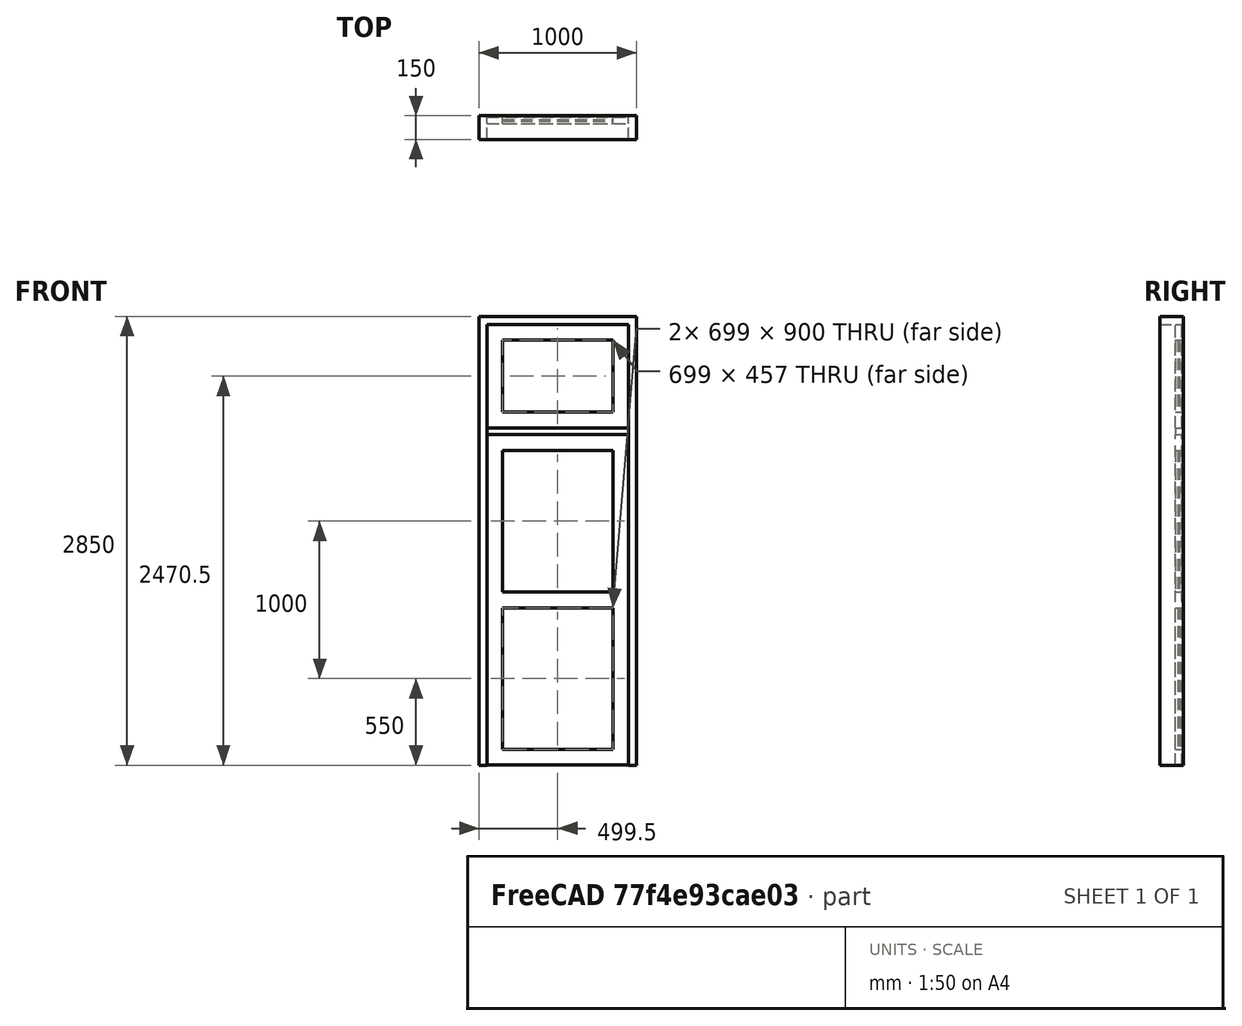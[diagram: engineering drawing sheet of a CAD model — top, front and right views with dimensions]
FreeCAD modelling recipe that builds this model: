
FCSTD DOCUMENT  (FreeCAD 0.16R6704 (Git))
Label: Single door with glass and transom
License: CreativeCommons Attribution
LicenseURL: http://creativecommons.org/licenses/by/4.0/
objects: Sketcher::SketchObject×1, Part::FeaturePython×1
note: 2 computed .brp shape members not serialized (recipe doc carries the construction recipe); baked Part::Feature solids carry a one-line shape summary decoded from their .brp

FEATURE [Sketcher::SketchObject] Sketch177  label="Sketch"
  Placement = pos=(0,0,0) rot=(1,0,0;1.5708rad)
  sketch-geometry (33):
    g0: LineSegment StartX=0 StartY=0 StartZ=0 EndX=1000 EndY=0 EndZ=0
    g1: LineSegment StartX=1000 StartY=0 StartZ=0 EndX=1000 EndY=2850 EndZ=0
    g2: LineSegment StartX=1000 StartY=2850 StartZ=0 EndX=0 EndY=2850 EndZ=0
    g3: LineSegment StartX=0 StartY=2850 StartZ=0 EndX=0 EndY=0 EndZ=0
    g4: LineSegment StartX=50 StartY=0 StartZ=0 EndX=950 EndY=0 EndZ=0
    g5: LineSegment StartX=950 StartY=0 StartZ=0 EndX=950 EndY=2800 EndZ=0
    g6: LineSegment StartX=950 StartY=2800 StartZ=0 EndX=50 EndY=2800 EndZ=0
    g7: LineSegment StartX=50 StartY=2800 StartZ=0 EndX=50 EndY=0 EndZ=0
    g8: LineSegment StartX=150 StartY=2000 StartZ=0 EndX=849 EndY=2000 EndZ=0
    g9: LineSegment StartX=849 StartY=2000 StartZ=0 EndX=849 EndY=1100 EndZ=0
    g10: LineSegment StartX=849 StartY=1100 StartZ=0 EndX=150 EndY=1100 EndZ=0
    g11: LineSegment StartX=150 StartY=1100 StartZ=0 EndX=150 EndY=2000 EndZ=0
    g12: LineSegment StartX=150 StartY=1000 StartZ=0 EndX=849 EndY=1000 EndZ=0
    g13: LineSegment StartX=849 StartY=1000 StartZ=0 EndX=849 EndY=100 EndZ=0
    g14: LineSegment StartX=849 StartY=100 StartZ=0 EndX=150 EndY=100 EndZ=0
    g15: LineSegment StartX=150 StartY=100 StartZ=0 EndX=150 EndY=1000 EndZ=0
    g16: LineSegment [constr] StartX=-278 StartY=1050 StartZ=0 EndX=1352 EndY=1050 EndZ=0
    g17: LineSegment StartX=51 StartY=2100 StartZ=0 EndX=949 EndY=2100 EndZ=0
    g18: LineSegment StartX=949 StartY=2100 StartZ=0 EndX=949 EndY=1 EndZ=0
    g19: LineSegment StartX=949 StartY=1 StartZ=0 EndX=51 EndY=1 EndZ=0
    g20: LineSegment StartX=51 StartY=1 StartZ=0 EndX=51 EndY=2100 EndZ=0
    g21: LineSegment StartX=51 StartY=2799 StartZ=0 EndX=949 EndY=2799 EndZ=0
    g22: LineSegment StartX=949 StartY=2799 StartZ=0 EndX=949 EndY=2142 EndZ=0
    g23: LineSegment StartX=949 StartY=2142 StartZ=0 EndX=51 EndY=2142 EndZ=0
    g24: LineSegment StartX=51 StartY=2142 StartZ=0 EndX=51 EndY=2799 EndZ=0
    g25: LineSegment StartX=150 StartY=2699 StartZ=0 EndX=849 EndY=2699 EndZ=0
    g26: LineSegment StartX=849 StartY=2699 StartZ=0 EndX=849 EndY=2242 EndZ=0
    g27: LineSegment StartX=849 StartY=2242 StartZ=0 EndX=150 EndY=2242 EndZ=0
    g28: LineSegment StartX=150 StartY=2242 StartZ=0 EndX=150 EndY=2699 EndZ=0
    g29: LineSegment StartX=51 StartY=2141 StartZ=0 EndX=949 EndY=2141 EndZ=0
    g30: LineSegment StartX=949 StartY=2141 StartZ=0 EndX=949 EndY=2101 EndZ=0
    g31: LineSegment StartX=949 StartY=2101 StartZ=0 EndX=51 EndY=2101 EndZ=0
    g32: LineSegment StartX=51 StartY=2101 StartZ=0 EndX=51 EndY=2141 EndZ=0
  constraints (97):
    c: Coincident(g0,g1)
    c: Coincident(g1,g2)
    c: Coincident(g2,g3)
    c: Coincident(g3,g0)
    c: Horizontal(g0)
    c: Horizontal(g2)
    c: Vertical(g1)
    c: Vertical(g3)
    c: Coincident(g4,g5)
    c: Coincident(g5,g6)
    c: Coincident(g6,g7)
    c: Coincident(g7,g4)
    c: Horizontal(g4)
    c: Horizontal(g6)
    c: Vertical(g5)
    c: Vertical(g7)
    c: DistanceY(g1) = 2850  'Altura do vão'
    c: DistanceX(g0) = 1000  'Largura do vão'
    c: DistanceY(g6,g2) = 50  'Batente horizontal'
    c: DistanceX(g2,g6) = 50  'Batente vertical 1'
    c: DistanceX(g4,g0) = 50  'Batente vertical 2'
    c: DistanceY(g0,g4) = 0
    c: Coincident(g0,g-1)
    c: Coincident(g8,g9)
    c: Coincident(g9,g10)
    c: Coincident(g10,g11)
    c: Coincident(g11,g8)
    c: Horizontal(g8)
    c: Horizontal(g10)
    c: Vertical(g9)
    c: Vertical(g11)
    c: Coincident(g12,g13)
    c: Coincident(g13,g14)
    c: Coincident(g14,g15)
    c: Coincident(g15,g12)
    c: Horizontal(g12)
    c: Horizontal(g14)
    c: Vertical(g13)
    c: Vertical(g15)
    c: DistanceX(g10,g12) = 0
    c: DistanceX(g9,g12) = 0
    c: DistanceY(g12,g10) = 100  'Moldura intermediária porta'
    c: DistanceX(g6,g8) = 100  'Moldura vertical 1 porta'
    c: DistanceY(g-1,g14) = 100  'Moldura inferior porta'
    c: Horizontal(g16)  'Constraint45'
    c: Symmetric(g10,g12,g16)
    c: DistanceY(g-1,g16) = 1050  'Altura montante intermediário porta ao chão (eixo)'
    c: Coincident(g17,g18)
    c: Coincident(g18,g19)
    c: Coincident(g19,g20)
    c: Coincident(g20,g17)
    c: Horizontal(g17)
    c: Horizontal(g19)
    c: Vertical(g18)
    c: Vertical(g20)
    c: DistanceX(g18,g4) = 1
    c: DistanceY(g4,g18) = 1
    c: DistanceX(g6,g17) = 1
    c: DistanceY(g8,g17) = 100  'Altura da moldura superior porta'
    c: Coincident(g21,g22)
    c: Coincident(g22,g23)
    c: Coincident(g23,g24)
    c: Coincident(g24,g21)
    c: Horizontal(g21)
    c: Horizontal(g23)
    c: Vertical(g22)
    c: Vertical(g24)
    c: Coincident(g25,g26)
    c: Coincident(g26,g27)
    c: Coincident(g27,g28)
    c: Coincident(g28,g25)
    c: Horizontal(g25)
    c: Horizontal(g27)
    c: Vertical(g26)
    c: Vertical(g28)
    c: DistanceY(g25,g21) = 100  'Altura moldura bandeira'
    c: DistanceY(g22,g26) = 100  'Altura da moldura bandeira 2'
    c: DistanceX(g8,g26) = 0  'Constraint80'
    c: DistanceY(g21,g6) = 1
    c: DistanceX(g8,g27) = 0
    c: DistanceY(g-1,g17) = 2100  'Altura da porta'
    c: Coincident(g29,g30)  'Constraint84'
    c: Coincident(g30,g31)
    c: Coincident(g31,g32)
    c: Horizontal(g29)
    c: Horizontal(g31)
    c: Vertical(g30)
    c: Vertical(g32)
    c: DistanceY(g17,g31) = 1
    c: DistanceX(g23,g29) = 0
    c: DistanceY(g29,g23) = 1
    c: DistanceX(g30,g17) = 0
    c: DistanceX(g22,g29) = 0
    c: DistanceX(g25,g21) = 100  'Largura moldura 2'
    c: DistanceX(g17,g31) = 0
    c: Coincident(g32,g29)
    c: DistanceY(g31,g29) = 40  'Batente bandeira'
FEATURE [Part::FeaturePython] Window110  label="Single door with glass and transom"  # WARN: FeaturePython — macro-defined, semantics opaque (R4)
  Base = -> Sketch177
  Height = 2100
  HoleDepth = 0
  MoveWithHost = true
  Normal = (0,1,0)
  Preset = 6
  Role = 1
  Width = 900
  WindowParts = BATENTE | Frame | Wire0,Wire1 | 150.0 | 0.0 | PORTA | Frame | Wire2,Wire3,Wire4 | 40.0 | 100.0 | BANDEIRA | Frame | Wire6,Wire5 | 40.0 | 100.0 | BATENTE BANDEIRA | Frame | Wire7 | 50.0 | 100.0 | VIDRO BANDEIRA | Glass panel | Wire6 | 10.0 | 115.0 | VIDRO SUPERIOR PORTA | Glass panel | Wire2 | 10.0 | 115.0 | VIDRO INFERIOR PORTA | Glass panel | Wire3 | 10.0 | 115.0
